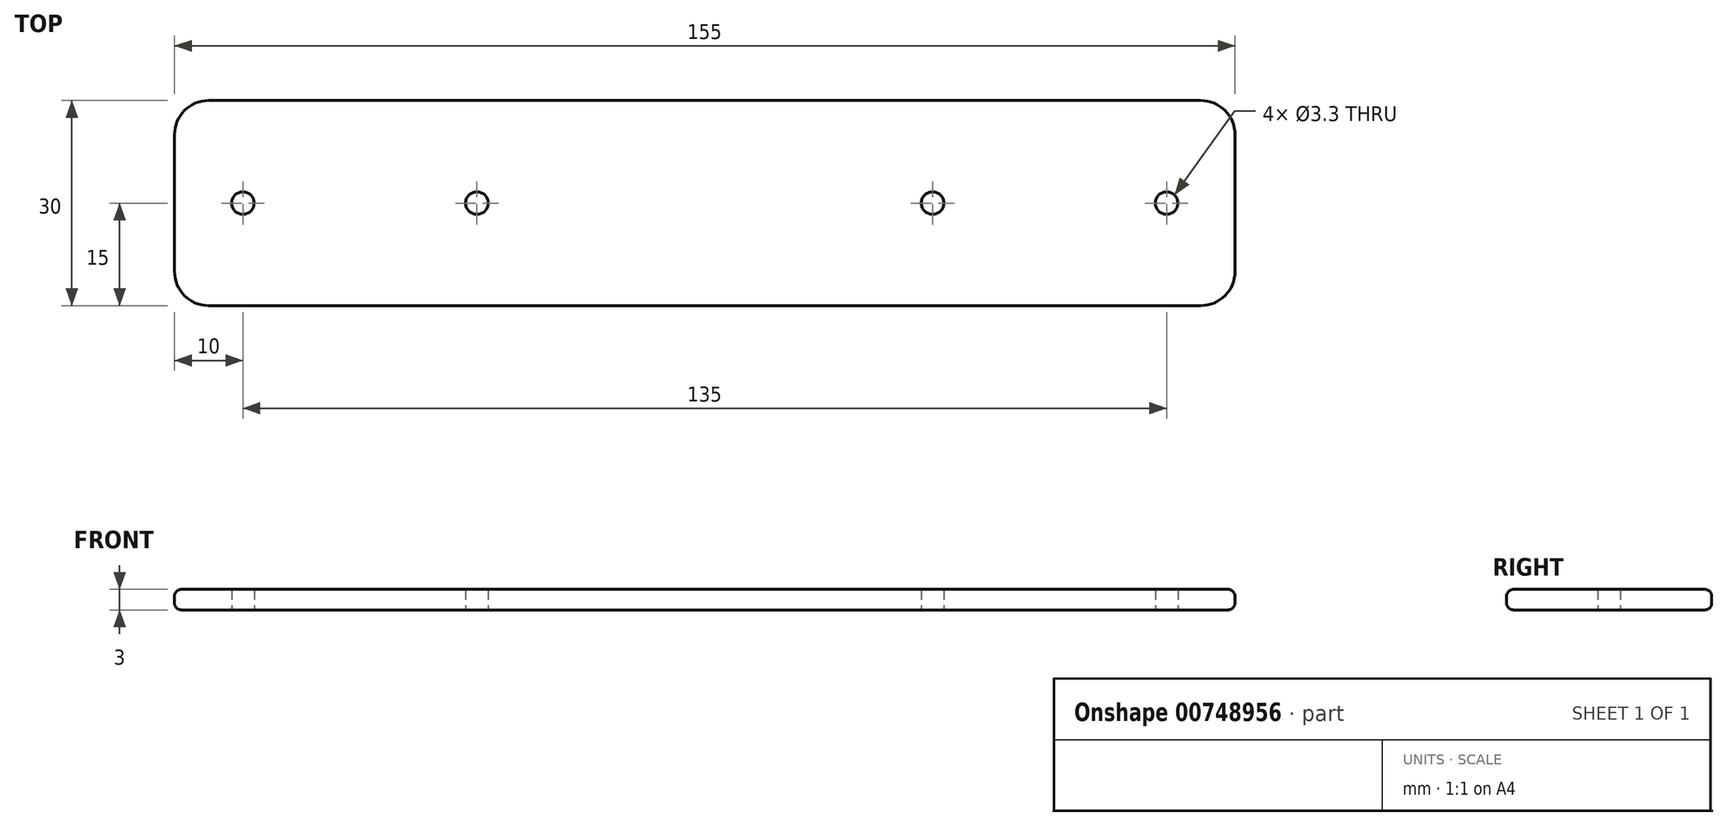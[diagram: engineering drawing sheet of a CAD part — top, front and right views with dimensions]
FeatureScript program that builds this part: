
annotation { "Feature Type Name" : "Feature", "Feature Type Description" : "" }
export const myFeature = defineFeature(function(context is Context, id is Id, definition is map)
    precondition{}
    {
        {
            var Q0;
            Q0=qCreatedBy(makeId("Top.planeOp"),FACE);
            var sketch = newSketch(context, id + "F0", { "sketchPlane" : qUnion([Q0])});
            skLineSegment(sketch, "E0.bottom", {"start": v(-77.5, 15) * mm, "end": v(77.5, 15) * mm});
            skLineSegment(sketch, "E0.top", {"start": v(-77.5, -15) * mm, "end": v(77.5, -15) * mm});
            skLineSegment(sketch, "E0.left", {"start": v(-77.5, 15) * mm, "end": v(-77.5, -15) * mm});
            skLineSegment(sketch, "E0.right", {"start": v(77.5, 15) * mm, "end": v(77.5, -15) * mm});
            skPoint(sketch, "E0.middle", {"position": v(0, 0) * mm});
            skPoint(sketch, "E1", {"position": v(-67.5, 0) * mm});
            skPoint(sketch, "E2", {"position": v(67.5, 0) * mm});
            skPoint(sketch, "E3", {"position": v(33.3, 0) * mm});
            skPoint(sketch, "E4", {"position": v(-33.3, 0) * mm});
            skSolve(sketch);
        }
        {
            var Q0;
            Q0=makeQuery(id+"F0.imprint","IMPRINT",FACE,{"disambiguationData":[TD([[makeQuery(id+"F0.imprint","IMPRINT",EDGE,{"derivedFrom":sQuery(id+"F0.wireOp",EDGE,"E0.bottom")}),-1.0]])]});
            extrude(context, id + "F1", {"entities" : qUnion([Q0]), "depth" : 3 * mm, "offsetDistance" : 25 * mm});
        }
        {
            var Q0;
            Q0=sQuery(id+"F0.wireOp",VERTEX,"E1");
            var Q1;
            Q1=sQuery(id+"F0.wireOp",VERTEX,"E2");
            var Q2;
            Q2=makeQuery(id+"F1.opExtrude","SWEPT_BODY",BODY,{"disambiguationData":[OSD([sQuery(id+"F0.wireOp",EDGE,"E0.bottom"),sQuery(id+"F0.wireOp",EDGE,"E0.top"),sQuery(id+"F0.wireOp",EDGE,"E0.left"),sQuery(id+"F0.wireOp",EDGE,"E0.right")])]});
            hole(context, id + "F2", {"style" : HoleStyle.SIMPLE, "endStyle" : HoleEndStyle.THROUGH, "oppositeDirection" : true, "standardTappedOrClearance" : lookupTablePath({ "standard" : "ISO", "fit" : "Normal", "size" : "M3", "type" : "Clearance" }), "standardBlindInLast" : lookupTablePath({ "fit" : "Standard", "standard" : "ISO", "size" : "M3", "type" : "Clearance" }), "holeDiameter" : 3.3 * mm, "majorDiameter" : 5 * mm, "isTappedThrough" : true, "tappedDepth" : 48.5 * mm, "tapClearance" : 3, "locations" : qUnion([Q0, Q1]), "scope" : qUnion([Q2])});
        }
        {
            var Q0;
            Q0=makeQuery(id+"F1.opExtrude","SWEPT_EDGE",EDGE,{"disambiguationData":[OSD([sQuery(id+"F0.wireOp",EDGE,"E0.bottom"),sQuery(id+"F0.wireOp",EDGE,"E0.left")])]});
            var Q1;
            Q1=makeQuery(id+"F1.opExtrude","SWEPT_EDGE",EDGE,{"disambiguationData":[OSD([sQuery(id+"F0.wireOp",EDGE,"E0.top"),sQuery(id+"F0.wireOp",EDGE,"E0.left")])]});
            var Q2;
            Q2=makeQuery(id+"F1.opExtrude","SWEPT_EDGE",EDGE,{"disambiguationData":[OSD([sQuery(id+"F0.wireOp",EDGE,"E0.top"),sQuery(id+"F0.wireOp",EDGE,"E0.right")])]});
            var Q3;
            Q3=makeQuery(id+"F1.opExtrude","SWEPT_EDGE",EDGE,{"disambiguationData":[OSD([sQuery(id+"F0.wireOp",EDGE,"E0.bottom"),sQuery(id+"F0.wireOp",EDGE,"E0.right")])]});
            fillet(context, id + "F3", {"entities" : qUnion([Q0, Q1, Q2, Q3]), "radius" : 5 * mm, "tangentPropagation" : true, "allowEdgeOverflow" : false});
        }
        {
            var Q0;
            Q0=makeQuery(id+"F1.opExtrude","CAP_EDGE",EDGE,{"disambiguationData":[OSD([sQuery(id+"F0.wireOp",EDGE,"E0.top")])],"isStart":false});
            var Q1;
            Q1=makeQuery(id+"F1.opExtrude","CAP_EDGE",EDGE,{"disambiguationData":[OSD([sQuery(id+"F0.wireOp",EDGE,"E0.top")])],"isStart":true});
            fillet(context, id + "F4", {"entities" : qUnion([Q0, Q1]), "radius" : 1 * mm, "tangentPropagation" : true, "allowEdgeOverflow" : false});
        }
        {
            var Q0;
            Q0=sQuery(id+"F0.wireOp",VERTEX,"E4");
            var Q1;
            Q1=sQuery(id+"F0.wireOp",VERTEX,"E3");
            var Q2;
            Q2=makeQuery(id+"F1.opExtrude","SWEPT_BODY",BODY,{"disambiguationData":[OSD([sQuery(id+"F0.wireOp",EDGE,"E0.bottom"),sQuery(id+"F0.wireOp",EDGE,"E0.top"),sQuery(id+"F0.wireOp",EDGE,"E0.left"),sQuery(id+"F0.wireOp",EDGE,"E0.right")])]});
            hole(context, id + "F5", {"style" : HoleStyle.SIMPLE, "endStyle" : HoleEndStyle.THROUGH, "oppositeDirection" : true, "standardTappedOrClearance" : lookupTablePath({ "standard" : "ISO", "fit" : "Normal", "size" : "M3", "type" : "Clearance" }), "standardBlindInLast" : lookupTablePath({ "fit" : "Standard", "standard" : "ISO", "size" : "M3", "type" : "Clearance" }), "holeDiameter" : 3.3 * mm, "majorDiameter" : 5 * mm, "isTappedThrough" : true, "tappedDepth" : 48.5 * mm, "tapClearance" : 3, "locations" : qUnion([Q0, Q1]), "scope" : qUnion([Q2])});
        }
    });
